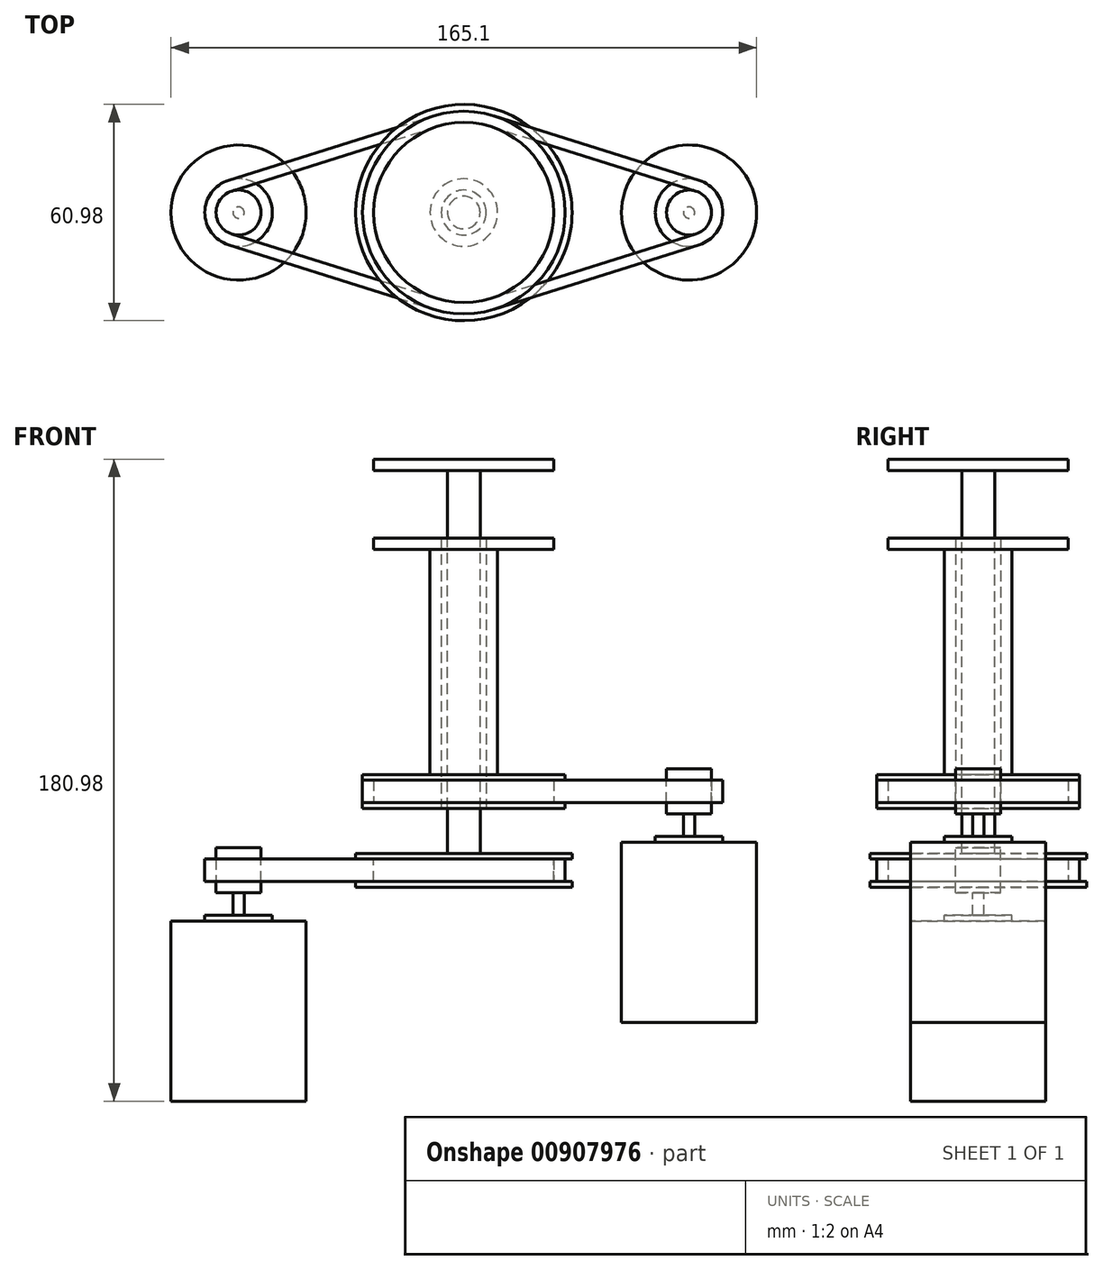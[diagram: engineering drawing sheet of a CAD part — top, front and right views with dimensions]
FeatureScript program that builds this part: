
annotation { "Feature Type Name" : "Feature", "Feature Type Description" : "" }
export const myFeature = defineFeature(function(context is Context, id is Id, definition is map)
    precondition{}
    {
        {
            var Q0;
            Q0=qCreatedBy(makeId("Front.planeOp"),FACE);
            var sketch = newSketch(context, id + "F0", { "sketchPlane" : qUnion([Q0])});
            skLineSegment(sketch, "E0", {"start": v(0, 0) * mm, "end": v(0, 76.2) * mm, "construction": true});
            skLineSegment(sketch, "E1", {"start": v(6.35, 76.2) * mm, "end": v(6.35, 0) * mm});
            skLineSegment(sketch, "E2", {"start": v(6.35, 0) * mm, "end": v(28.58, 0) * mm});
            skLineSegment(sketch, "E3", {"start": v(28.58, 0) * mm, "end": v(28.58, 1.59) * mm});
            skLineSegment(sketch, "E4", {"start": v(28.58, 1.59) * mm, "end": v(25.4, 1.59) * mm});
            skLineSegment(sketch, "E5", {"start": v(25.4, 1.59) * mm, "end": v(25.4, 7.94) * mm});
            skLineSegment(sketch, "E6", {"start": v(25.4, 7.94) * mm, "end": v(28.58, 7.94) * mm});
            skLineSegment(sketch, "E7", {"start": v(28.58, 7.94) * mm, "end": v(28.58, 9.52) * mm});
            skLineSegment(sketch, "E8", {"start": v(28.58, 9.53) * mm, "end": v(9.52, 9.53) * mm});
            skLineSegment(sketch, "E9", {"start": v(9.52, 9.52) * mm, "end": v(9.52, 73.03) * mm});
            skLineSegment(sketch, "E10", {"start": v(9.52, 73.03) * mm, "end": v(25.4, 73.03) * mm});
            skLineSegment(sketch, "E11", {"start": v(25.4, 73.03) * mm, "end": v(25.4, 76.2) * mm});
            skLineSegment(sketch, "E12", {"start": v(25.4, 76.2) * mm, "end": v(6.35, 76.2) * mm});
            skSolve(sketch);
        }
        {
            var Q0;
            Q0=makeQuery(id+"F0.imprint","IMPRINT",FACE,{"disambiguationData":[TD([[makeQuery(id+"F0.imprint","IMPRINT",EDGE,{"derivedFrom":sQuery(id+"F0.wireOp",EDGE,"E1")}),1.0]])]});
            var Q1;
            Q1=sQuery(id+"F0.wireOp",EDGE,"E0");
            revolve(context, id + "F1", {"surfaceOperationType" : NewSurfaceOperationType.NEW, "entities" : qUnion([Q0]), "axis" : qUnion([Q1]), "revolveType" : RevolveType.FULL});
        }
        {
            var Q0;
            Q0=qCreatedBy(makeId("Front.planeOp"),FACE);
            var sketch = newSketch(context, id + "F2", { "sketchPlane" : qUnion([Q0])});
            skLineSegment(sketch, "E13", {"start": v(0, -22.23) * mm, "end": v(30.5, -22.23) * mm});
            skLineSegment(sketch, "E14", {"start": v(30.5, -22.23) * mm, "end": v(30.5, -20.64) * mm});
            skLineSegment(sketch, "E15", {"start": v(30.5, -20.64) * mm, "end": v(25.4, -20.64) * mm});
            skLineSegment(sketch, "E16", {"start": v(25.4, -20.64) * mm, "end": v(25.4, -14.29) * mm});
            skLineSegment(sketch, "E17", {"start": v(25.4, -14.29) * mm, "end": v(30.5, -14.29) * mm});
            skLineSegment(sketch, "E18", {"start": v(30.5, -14.29) * mm, "end": v(30.5, -12.7) * mm});
            skLineSegment(sketch, "E19", {"start": v(30.5, -12.7) * mm, "end": v(4.59, -12.7) * mm});
            skLineSegment(sketch, "E20", {"start": v(4.59, -12.7) * mm, "end": v(4.59, 95.25) * mm});
            skLineSegment(sketch, "E21", {"start": v(4.59, 95.25) * mm, "end": v(25.4, 95.25) * mm});
            skLineSegment(sketch, "E22", {"start": v(25.4, 95.25) * mm, "end": v(25.4, 98.42) * mm});
            skLineSegment(sketch, "E23", {"start": v(25.4, 98.42) * mm, "end": v(0, 98.42) * mm});
            skLineSegment(sketch, "E24", {"start": v(0, 98.42) * mm, "end": v(0, -22.23) * mm});
            skSolve(sketch);
        }
        {
            var Q0;
            Q0=makeQuery(id+"F2.imprint","IMPRINT",FACE,{"disambiguationData":[TD([[makeQuery(id+"F2.imprint","IMPRINT",EDGE,{"derivedFrom":sQuery(id+"F2.wireOp",EDGE,"E13")}),1.0]])]});
            var Q1;
            Q1=sQuery(id+"F2.wireOp",EDGE,"E24");
            revolve(context, id + "F3", {"surfaceOperationType" : NewSurfaceOperationType.NEW, "entities" : qUnion([Q0]), "axis" : qUnion([Q1]), "revolveType" : RevolveType.FULL});
        }
        {
            var Q0;
            Q0=makeQuery(id+"F3.opRevolve","SWEPT_FACE",FACE,{"disambiguationData":[OSD([sQuery(id+"F2.wireOp",EDGE,"E15")])]});
            var sketch = newSketch(context, id + "F4", { "sketchPlane" : qUnion([Q0])});
            skArc(sketch, "E25", {"start": v(-7.62, -24.23) * mm, "mid": v(25.4, 0) * mm, "end": v(-7.62, 24.23) * mm});
            skLineSegment(sketch, "E26", {"start": v(0, 0) * mm, "end": v(-63.5, 0) * mm, "construction": true});
            skArc(sketch, "E27", {"start": v(-65.4, 6.06) * mm, "mid": v(-69.85, 0) * mm, "end": v(-65.4, -6.06) * mm});
            skLineSegment(sketch, "E28", {"start": v(-65.4, 6.06) * mm, "end": v(-7.62, 24.23) * mm});
            skLineSegment(sketch, "E29.MirrorCS", {"start": v(-65.4, -6.06) * mm, "end": v(-7.62, -24.23) * mm});
            skLineSegment(sketch, "E30.0", {"start": v(-66.36, 9.09) * mm, "end": v(-8.57, 27.26) * mm});
            skArc(sketch, "E30.1", {"start": v(-66.36, 9.09) * mm, "mid": v(-73.03, 0) * mm, "end": v(-66.36, -9.09) * mm});
            skLineSegment(sketch, "E30.2", {"start": v(-66.36, -9.09) * mm, "end": v(-8.57, -27.26) * mm});
            skArc(sketch, "E30.3", {"start": v(-8.57, -27.26) * mm, "mid": v(28.57, 0) * mm, "end": v(-8.57, 27.26) * mm});
            skSolve(sketch);
        }
        {
            var Q0;
            Q0 = qSketchRegion(id + "F4", true);
            extrude(context, id + "F5", {"entities" : qUnion([Q0]), "depth" : 6.35 * mm, "offsetDistance" : 25.4 * mm});
        }
        {
            var Q0;
            Q0=makeQuery(id+"F1.opRevolve","SWEPT_FACE",FACE,{"disambiguationData":[OSD([sQuery(id+"F0.wireOp",EDGE,"E4")])]});
            var sketch = newSketch(context, id + "F6", { "sketchPlane" : qUnion([Q0])});
            skLineSegment(sketch, "E31", {"start": v(0, 0) * mm, "end": v(63.5, 0) * mm, "construction": true});
            skArc(sketch, "E32", {"start": v(65.4, -6.06) * mm, "mid": v(69.85, 0) * mm, "end": v(65.4, 6.06) * mm});
            skLineSegment(sketch, "E33", {"start": v(7.62, -24.23) * mm, "end": v(65.4, -6.06) * mm});
            skLineSegment(sketch, "E34.MirrorCS", {"start": v(7.62, 24.23) * mm, "end": v(65.4, 6.06) * mm});
            skArc(sketch, "E35", {"start": v(7.62, 24.23) * mm, "mid": v(-25.4, 0) * mm, "end": v(7.62, -24.23) * mm});
            skLineSegment(sketch, "E36.0", {"start": v(8.57, 27.26) * mm, "end": v(66.36, 9.09) * mm});
            skArc(sketch, "E36.1", {"start": v(8.57, 27.26) * mm, "mid": v(-28.58, 0) * mm, "end": v(8.57, -27.26) * mm});
            skLineSegment(sketch, "E36.2", {"start": v(8.57, -27.26) * mm, "end": v(66.36, -9.09) * mm});
            skArc(sketch, "E36.3", {"start": v(66.36, -9.09) * mm, "mid": v(73.03, 0) * mm, "end": v(66.36, 9.09) * mm});
            skSolve(sketch);
        }
        {
            var Q0;
            Q0 = qSketchRegion(id + "F6", true);
            extrude(context, id + "F7", {"entities" : qUnion([Q0]), "depth" : 6.35 * mm, "offsetDistance" : 25.4 * mm});
        }
        {
            var Q0;
            Q0=qCreatedBy(makeId("Front.planeOp"),FACE);
            var sketch = newSketch(context, id + "F8", { "sketchPlane" : qUnion([Q0])});
            skLineSegment(sketch, "E37", {"start": v(-63.5, 15.8) * mm, "end": v(-63.5, -57.07) * mm, "construction": true});
            skLineSegment(sketch, "E38", {"start": v(-63.5, -11.11) * mm, "end": v(-69.85, -11.11) * mm});
            skLineSegment(sketch, "E39", {"start": v(-69.85, -11.11) * mm, "end": v(-69.85, -23.81) * mm});
            skLineSegment(sketch, "E40", {"start": v(-69.85, -23.81) * mm, "end": v(-65.09, -23.81) * mm});
            skLineSegment(sketch, "E41", {"start": v(-65.09, -23.81) * mm, "end": v(-65.09, -30.16) * mm});
            skLineSegment(sketch, "E42", {"start": v(-65.09, -30.16) * mm, "end": v(-73.03, -30.16) * mm});
            skLineSegment(sketch, "E43", {"start": v(-73.03, -30.16) * mm, "end": v(-73.03, -31.75) * mm});
            skLineSegment(sketch, "E44", {"start": v(-73.03, -31.75) * mm, "end": v(-82.55, -31.75) * mm});
            skLineSegment(sketch, "E45", {"start": v(-82.55, -31.75) * mm, "end": v(-82.55, -82.55) * mm});
            skLineSegment(sketch, "E46", {"start": v(-82.55, -82.55) * mm, "end": v(-63.5, -82.55) * mm});
            skLineSegment(sketch, "E47", {"start": v(-63.5, -82.55) * mm, "end": v(-63.5, -11.11) * mm});
            skSolve(sketch);
        }
        {
            var Q0;
            Q0=makeQuery(id+"F8.imprint","IMPRINT",FACE,{"disambiguationData":[TD([[makeQuery(id+"F8.imprint","IMPRINT",EDGE,{"derivedFrom":sQuery(id+"F8.wireOp",EDGE,"E38")}),1.0]])]});
            var Q1;
            Q1=sQuery(id+"F8.wireOp",EDGE,"E37");
            revolve(context, id + "F9", {"surfaceOperationType" : NewSurfaceOperationType.NEW, "entities" : qUnion([Q0]), "axis" : qUnion([Q1]), "revolveType" : RevolveType.FULL});
        }
        {
            var Q0;
            Q0=qCreatedBy(makeId("Front.planeOp"),FACE);
            var sketch = newSketch(context, id + "F10", { "sketchPlane" : qUnion([Q0])});
            skLineSegment(sketch, "E48", {"start": v(63.5, 26.1) * mm, "end": v(63.5, -36.69) * mm, "construction": true});
            skLineSegment(sketch, "E49", {"start": v(63.5, 11.11) * mm, "end": v(69.85, 11.11) * mm});
            skLineSegment(sketch, "E50", {"start": v(69.85, 11.11) * mm, "end": v(69.85, -1.59) * mm});
            skLineSegment(sketch, "E51", {"start": v(69.85, -1.59) * mm, "end": v(65.09, -1.59) * mm});
            skLineSegment(sketch, "E52", {"start": v(65.09, -1.59) * mm, "end": v(65.09, -7.94) * mm});
            skLineSegment(sketch, "E53", {"start": v(65.09, -7.94) * mm, "end": v(73.03, -7.94) * mm});
            skLineSegment(sketch, "E54", {"start": v(73.03, -7.94) * mm, "end": v(73.03, -9.52) * mm});
            skLineSegment(sketch, "E55", {"start": v(73.03, -9.52) * mm, "end": v(82.55, -9.52) * mm});
            skLineSegment(sketch, "E56", {"start": v(82.55, -9.52) * mm, "end": v(82.55, -60.33) * mm});
            skLineSegment(sketch, "E57", {"start": v(82.55, -60.33) * mm, "end": v(63.5, -60.33) * mm});
            skLineSegment(sketch, "E58", {"start": v(63.5, -60.33) * mm, "end": v(63.5, 11.11) * mm});
            skSolve(sketch);
        }
        {
            var Q0;
            Q0=makeQuery(id+"F10.imprint","IMPRINT",FACE,{"disambiguationData":[TD([[makeQuery(id+"F10.imprint","IMPRINT",EDGE,{"derivedFrom":sQuery(id+"F10.wireOp",EDGE,"E49")}),-1.0]])]});
            var Q1;
            Q1=sQuery(id+"F10.wireOp",EDGE,"E48");
            revolve(context, id + "F11", {"surfaceOperationType" : NewSurfaceOperationType.NEW, "entities" : qUnion([Q0]), "axis" : qUnion([Q1]), "revolveType" : RevolveType.FULL});
        }
    });
